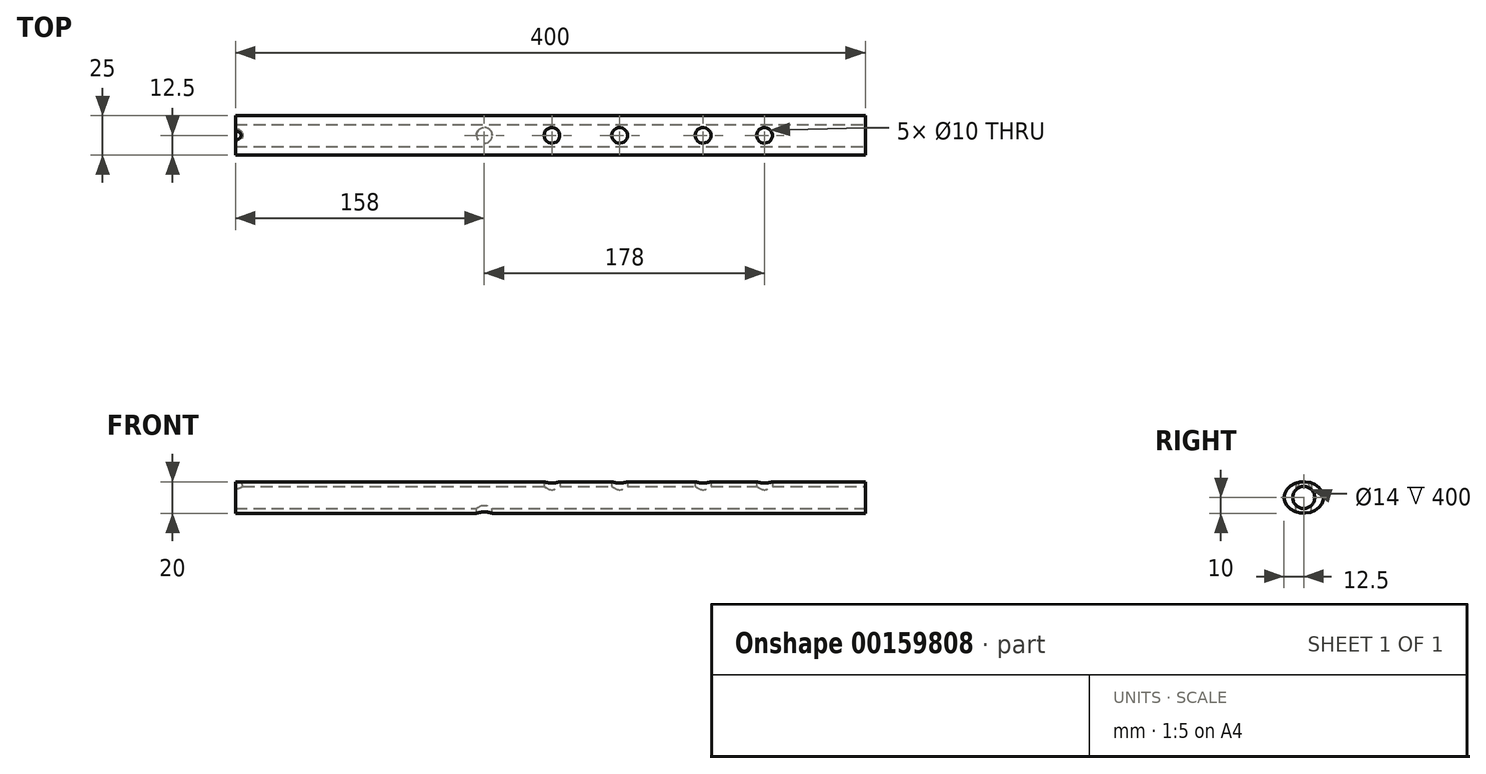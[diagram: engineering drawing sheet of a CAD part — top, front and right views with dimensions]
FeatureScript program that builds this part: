
annotation { "Feature Type Name" : "Feature", "Feature Type Description" : "" }
export const myFeature = defineFeature(function(context is Context, id is Id, definition is map)
    precondition{}
    {
        {
            var Q0;
            Q0=qCreatedBy(makeId("Right.planeOp"),FACE);
            var sketch = newSketch(context, id + "F0", { "sketchPlane" : qUnion([Q0])});
            skCircle(sketch, "E0", {"center": v(0, 0) * mm, "radius": 7 * mm, "construction": true});
            skEllipse(sketch, "E1", {"center": v(0, 0) * mm, "majorRadius": 12.5 * mm, "minorRadius": 10 * mm, "majorAxis": v(-1, 0)});
            skSolve(sketch);
        }
        {
            var Q0;
            Q0 = qSketchRegion(id + "F0", true);
            extrude(context, id + "F1", {"entities" : qUnion([Q0]), "depth" : 400 * mm});
        }
        {
            var Q0;
            Q0=makeQuery(id+"F1.opExtrude","CAP_FACE",FACE,{"disambiguationData":[OSD([sQuery(id+"F0.wireOp",EDGE,"E0"),sQuery(id+"F0.wireOp",EDGE,"E1")])],"isStart":false});
            var sketch = newSketch(context, id + "F2", { "sketchPlane" : qUnion([Q0])});
            skCircle(sketch, "E2", {"center": v(0, 0) * mm, "radius": 7 * mm});
            skSolve(sketch);
        }
        {
            var Q0;
            Q0=qCreatedBy(makeId("Right.planeOp"),FACE);
            var sketch = newSketch(context, id + "F3", { "sketchPlane" : qUnion([Q0])});
            skCircle(sketch, "E3.0", {"center": v(0, 0) * mm, "radius": 7 * mm});
            skSolve(sketch);
        }
        {
            var Q1;
            Q1=makeQuery(id+"F2.imprint","IMPRINT",FACE,{"disambiguationData":[TD([[makeQuery(id+"F2.imprint","IMPRINT",EDGE,{"derivedFrom":sQuery(id+"F2.wireOp",EDGE,"E2")}),1.0]])]});
            var Q2;
            Q2=makeQuery(id+"F3.imprint","IMPRINT",FACE,{"disambiguationData":[TD([[makeQuery(id+"F3.imprint","IMPRINT",EDGE,{"derivedFrom":sQuery(id+"F3.wireOp",EDGE,"E3.0")}),1.0]])]});
            var Q3;
            Q3=sQuery(id+"F3.wireOp",EDGE,"E3.0");
            var Q4;
            Q4=sQuery(id+"F2.wireOp",EDGE,"E2");
            loft(context, id + "F4", {"operationType" : NewBodyOperationType.REMOVE, "sheetProfilesArray" : [{ "sheetProfileEntities" : qUnion([Q1]) }, { "sheetProfileEntities" : qUnion([Q2]) }], "wireProfilesArray" : [{ "wireProfileEntities" : qUnion([Q3]) }, { "wireProfileEntities" : qUnion([Q4]) }]});
        }
        {
            var Q0;
            Q0=qCreatedBy(makeId("Top.planeOp"),FACE);
            var sketch = newSketch(context, id + "F10", { "sketchPlane" : qUnion([Q0])});
            skCircle(sketch, "E4", {"center": v(201, 0) * mm, "radius": 5 * mm});
            skCircle(sketch, "E5", {"center": v(244, 0) * mm, "radius": 5 * mm});
            skCircle(sketch, "E6", {"center": v(297, 0) * mm, "radius": 5 * mm});
            skCircle(sketch, "E7", {"center": v(336, 0) * mm, "radius": 5 * mm});
            skCircle(sketch, "E8", {"center": v(158, 0) * mm, "radius": 5 * mm});
            skSolve(sketch);
        }
        {
            var Q0;
            Q0=qCreatedBy(makeId("Front.planeOp"),FACE);
            var sketch = newSketch(context, id + "F5", { "sketchPlane" : qUnion([Q0])});
            skLineSegment(sketch, "E9", {"start": v(10, 0) * mm, "end": v(-3.48, 13.48) * mm});
            skLineSegment(sketch, "E10", {"start": v(10, 0) * mm, "end": v(0, 0) * mm, "construction": true});
            skSolve(sketch);
        }
        {
            var Q0;
            Q0=makeQuery(id+"F10.imprint","IMPRINT",FACE,{"disambiguationData":[TD([[makeQuery(id+"F10.imprint","IMPRINT",EDGE,{"derivedFrom":sQuery(id+"F10.wireOp",EDGE,"E7")}),1.0]])]});
            var Q1;
            Q1=makeQuery(id+"F10.imprint","IMPRINT",FACE,{"disambiguationData":[TD([[makeQuery(id+"F10.imprint","IMPRINT",EDGE,{"derivedFrom":sQuery(id+"F10.wireOp",EDGE,"E6")}),1.0]])]});
            var Q2;
            Q2=makeQuery(id+"F10.imprint","IMPRINT",FACE,{"disambiguationData":[TD([[makeQuery(id+"F10.imprint","IMPRINT",EDGE,{"derivedFrom":sQuery(id+"F10.wireOp",EDGE,"E5")}),1.0]])]});
            var Q3;
            Q3=makeQuery(id+"F10.imprint","IMPRINT",FACE,{"disambiguationData":[TD([[makeQuery(id+"F10.imprint","IMPRINT",EDGE,{"derivedFrom":sQuery(id+"F10.wireOp",EDGE,"E4")}),1.0]])]});
            extrude(context, id + "F6", {"entities" : qUnion([Q0, Q1, Q2, Q3]), "operationType" : NewBodyOperationType.REMOVE, "depth" : 25 * mm});
        }
        {
            var Q0;
            Q0=makeQuery(id+"F10.imprint","IMPRINT",FACE,{"disambiguationData":[TD([[makeQuery(id+"F10.imprint","IMPRINT",EDGE,{"derivedFrom":sQuery(id+"F10.wireOp",EDGE,"E8")}),1.0]])]});
            extrude(context, id + "F11", {"entities" : qUnion([Q0]), "operationType" : NewBodyOperationType.REMOVE, "oppositeDirection" : true, "depth" : 25 * mm});
        }
        {
            var Q0;
            Q0=qCreatedBy(makeId("Top.planeOp"),FACE);
            cPlane(context, id + "F7", {"entities" : qUnion([Q0]), "cplaneType" : CPlaneType.OFFSET, "offset" : 3 * mm, "width" : 150 * mm, "height" : 150 * mm});
        }
        {
            var Q0;
            Q0=qCreatedBy(id+"F7.planeOp",FACE);
            var sketch = newSketch(context, id + "F8", { "sketchPlane" : qUnion([Q0])});
            skArc(sketch, "E11", {"start": v(1.44, -4.98) * mm, "mid": v(6, 0) * mm, "end": v(1.44, 4.98) * mm});
            skLineSegment(sketch, "E12", {"start": v(1.44, 4.98) * mm, "end": v(-4, 5.46) * mm});
            skLineSegment(sketch, "E13", {"start": v(-4, 5.46) * mm, "end": v(-4, -5.46) * mm});
            skLineSegment(sketch, "E14", {"start": v(-4, -5.46) * mm, "end": v(1.44, -4.98) * mm});
            skSolve(sketch);
        }
        {
            var Q0;
            Q0 = qSketchRegion(id + "F8", true);
            extrude(context, id + "F9", {"entities" : qUnion([Q0]), "operationType" : NewBodyOperationType.REMOVE, "endBound" : BoundingType.THROUGH_ALL, "depth" : 25 * mm, "hasDraft" : true, "draftAngle" : 20 * degree, "draftPullDirection" : true, "offsetDistance" : 25 * mm});
        }
    });
